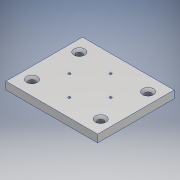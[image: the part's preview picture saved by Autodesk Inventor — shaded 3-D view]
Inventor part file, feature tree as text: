
AUTODESK INVENTOR PART (.ipt)
format: ipt  version: 2017 (Build 210142000, 142)  size: 131,584 bytes
history: native  units: mm
features: chamfer x3, sketch x3, hole x2, extrude x1
ambient origin geometry x8: Origin, YZ Plane, XZ Plane, XY Plane, X Axis, Y Axis, Z Axis, Center Point
bodies: Solid1 (feature_tree)
feature tree (9):
  extrude  "Extrusion1"  Depth=100.0mm
  hole  "Hole1"  [1 undecoded]
  chamfer  "Chamfer1"  Distance=3.0mm Angle=45.0deg
  chamfer  "Chamfer2"  Distance=3.0mm Angle=45.0deg
  hole  "Hole2"  [1 undecoded]
  chamfer  "Chamfer3"  Distance=40.0mm Angle=360.0deg
  sketch  "Sketch1"  dims[d0=120.0mm d1=100.0mm]
  sketch  "Sketch2"  dims[d3=10.0mm d4=0.0mm d5=90.0mm]
  sketch  "Sketch3"  dims[d6=62.0mm d7=8.0mm d8=6.0mm d9=4.0mm d10=2.0mm d11=90.0deg d12=8.0mm d13=20.594885mm d14=3.0mm d15=2.0mm d16=45.0deg d17=3.0mm d18=2.0mm d19=45.0deg d20=54.0mm d21=40.0mm d23=360.0deg d25=3.0mm d26=6.0mm d27=4.0mm d28=2.0mm d29=90.0deg d30=8.0mm d31=20.594885mm d32=2.0mm d33=2.0mm d34=45.0deg]
note: 2 required parameter values undecoded (feature->parameter linkage not recoverable at this tier; creation-order binding heuristic only, values carry confidence <= 0.55)
